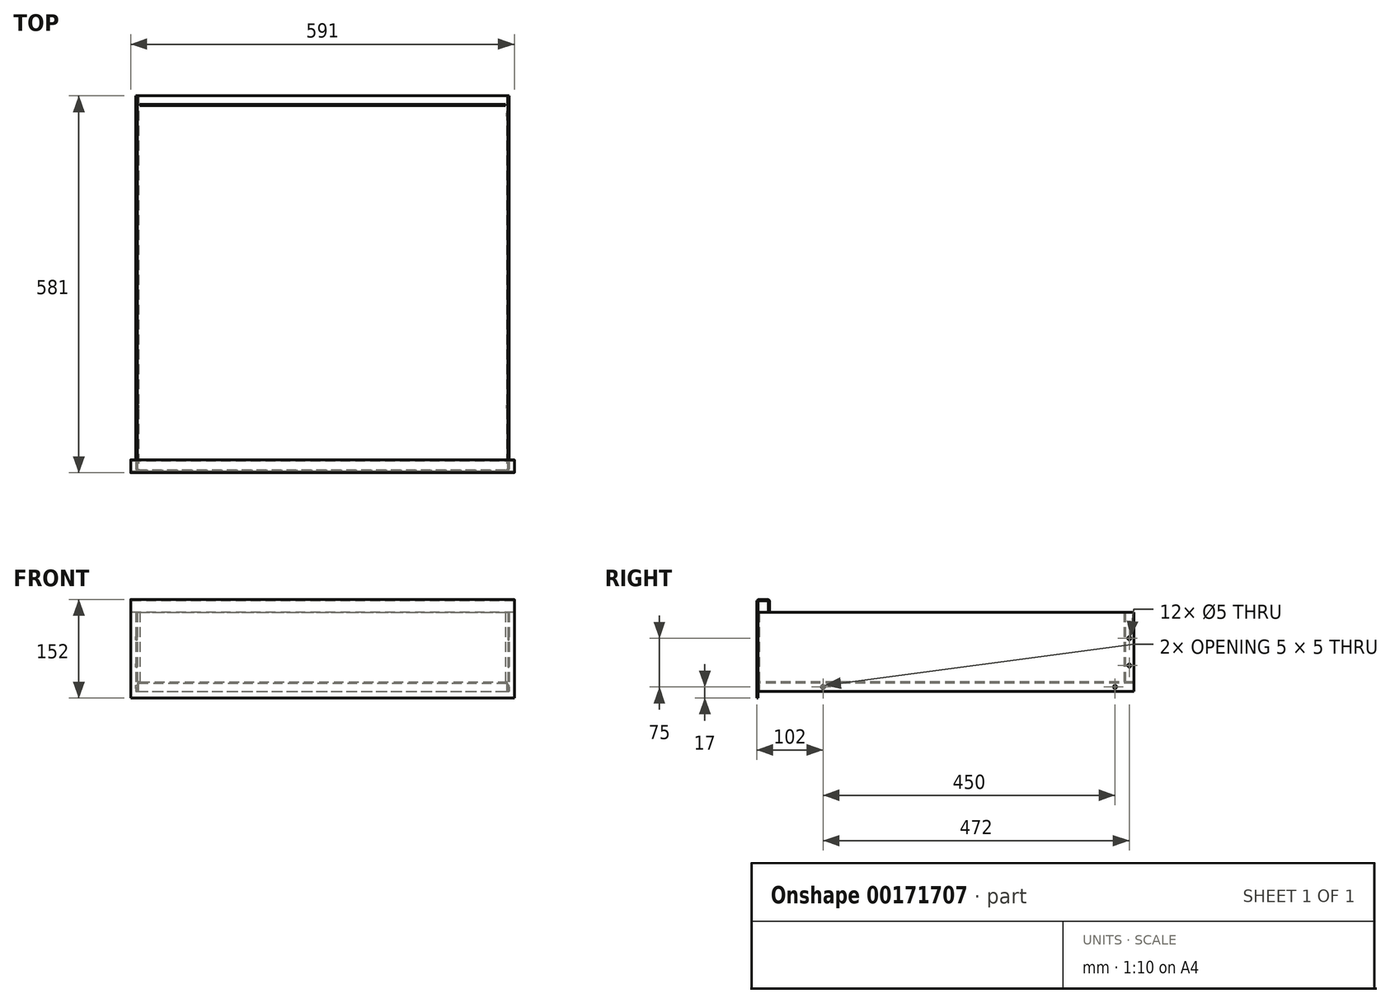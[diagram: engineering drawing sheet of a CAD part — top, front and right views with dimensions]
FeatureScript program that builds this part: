
annotation { "Feature Type Name" : "Feature", "Feature Type Description" : "" }
export const myFeature = defineFeature(function(context is Context, id is Id, definition is map)
    precondition{}
    {
        {
            var Q0;
            Q0=qCreatedBy(makeId("Top.planeOp"),FACE);
            var sketch = newSketch(context, id + "F0", { "sketchPlane" : qUnion([Q0])});
            skLineSegment(sketch, "E0.top", {"start": v(-283.5, -289.5) * mm, "end": v(283.5, -289.5) * mm});
            skLineSegment(sketch, "E0.left", {"start": v(-287.5, 289.5) * mm, "end": v(-287.5, -285.5) * mm});
            skLineSegment(sketch, "E0.right", {"start": v(287.5, 289.5) * mm, "end": v(287.5, -285.5) * mm});
            skPoint(sketch, "E0.middle", {"position": v(0, 0) * mm});
            skLineSegment(sketch, "E1", {"start": v(-287.5, 289.5) * mm, "end": v(287.5, 289.5) * mm, "construction": true});
            skLineSegment(sketch, "E2", {"start": v(-287.5, 289.5) * mm, "end": v(-285.5, 289.5) * mm});
            skLineSegment(sketch, "E3", {"start": v(-285.5, 289.5) * mm, "end": v(-285.5, -287.5) * mm});
            skLineSegment(sketch, "E4", {"start": v(-285.5, -287.5) * mm, "end": v(285.5, -287.5) * mm});
            skLineSegment(sketch, "E5", {"start": v(285.5, -287.5) * mm, "end": v(285.5, 289.5) * mm});
            skPoint(sketch, "E6.visualSharp", {"position": v(-287.5, -289.5) * mm});
            skArc(sketch, "E6.filletArc", {"start": v(-287.5, -285.5) * mm, "mid": v(-286.33, -288.33) * mm, "end": v(-283.5, -289.5) * mm});
            skPoint(sketch, "E7.visualSharp", {"position": v(287.5, -289.5) * mm});
            skArc(sketch, "E7.filletArc", {"start": v(283.5, -289.5) * mm, "mid": v(286.33, -288.33) * mm, "end": v(287.5, -285.5) * mm});
            skLineSegment(sketch, "E8", {"start": v(285.5, 289.5) * mm, "end": v(287.5, 289.5) * mm});
            skSolve(sketch);
        }
        {
            var Q0;
            Q0=makeQuery(id+"F0.imprint","IMPRINT",FACE,{"disambiguationData":[TD([[makeQuery(id+"F0.imprint","IMPRINT",EDGE,{"derivedFrom":sQuery(id+"F0.wireOp",EDGE,"E0.top")}),1.0]])]});
            extrude(context, id + "F1", {"entities" : qUnion([Q0]), "depth" : 122 * mm});
        }
        {
            var Q0;
            Q0=makeQuery(id+"F1.opExtrude","SWEPT_FACE",FACE,{"disambiguationData":[OSD([sQuery(id+"F0.wireOp",EDGE,"E4")])]});
            var sketch = newSketch(context, id + "F2", { "sketchPlane" : qUnion([Q0])});
            skLineSegment(sketch, "E9", {"start": v(-285.5, 0) * mm, "end": v(-285.5, 11) * mm});
            skLineSegment(sketch, "E10", {"start": v(-281.5, 15) * mm, "end": v(281.5, 15) * mm});
            skLineSegment(sketch, "E11", {"start": v(285.5, 11) * mm, "end": v(285.5, 0) * mm});
            skLineSegment(sketch, "E12", {"start": v(285.5, 0) * mm, "end": v(283.5, 0) * mm});
            skLineSegment(sketch, "E13", {"start": v(283.5, 0) * mm, "end": v(283.5, 13) * mm});
            skLineSegment(sketch, "E14", {"start": v(283.5, 13) * mm, "end": v(-283.5, 13) * mm});
            skLineSegment(sketch, "E15", {"start": v(-283.5, 13) * mm, "end": v(-283.5, 0) * mm});
            skLineSegment(sketch, "E16", {"start": v(-283.5, 0) * mm, "end": v(-285.5, 0) * mm});
            skPoint(sketch, "E17.visualSharp", {"position": v(285.5, 15) * mm});
            skArc(sketch, "E17.filletArc", {"start": v(285.5, 11) * mm, "mid": v(284.33, 13.83) * mm, "end": v(281.5, 15) * mm});
            skPoint(sketch, "E18.visualSharp", {"position": v(-285.5, 15) * mm});
            skArc(sketch, "E18.filletArc", {"start": v(-281.5, 15) * mm, "mid": v(-284.33, 13.83) * mm, "end": v(-285.5, 11) * mm});
            skSolve(sketch);
        }
        {
            var Q0;
            Q0=makeQuery(id+"F2.imprint","IMPRINT",FACE,{"disambiguationData":[TD([[makeQuery(id+"F2.imprint","IMPRINT",EDGE,{"derivedFrom":sQuery(id+"F2.wireOp",EDGE,"E9")}),1.0]])]});
            var Q1;
            Q1=makeQuery(id+"F1.opExtrude","SWEPT_FACE",FACE,{"disambiguationData":[OSD([sQuery(id+"F0.wireOp",EDGE,"E2")])]});
            extrude(context, id + "F3", {"entities" : qUnion([Q0]), "endBound" : BoundingType.UP_TO_SURFACE, "endBoundEntityFace" : qUnion([Q1]), "depth" : 25 * mm});
        }
        {
            var Q0;
            Q0=makeQuery(id+"F3.opExtrude","SWEPT_FACE",FACE,{"disambiguationData":[OSD([sQuery(id+"F2.wireOp",EDGE,"E10")])]});
            var sketch = newSketch(context, id + "F4", { "sketchPlane" : qUnion([Q0])});
            skLineSegment(sketch, "E19.0", {"start": v(285.5, -287.5) * mm, "end": v(285.5, 289.5) * mm});
            skLineSegment(sketch, "E20.0", {"start": v(-285.5, 289.5) * mm, "end": v(-285.5, -287.5) * mm});
            skLineSegment(sketch, "E21", {"start": v(-285.5, 289.5) * mm, "end": v(-285.5, 278.5) * mm});
            skLineSegment(sketch, "E22", {"start": v(-281.5, 274.5) * mm, "end": v(281.5, 274.5) * mm});
            skLineSegment(sketch, "E23", {"start": v(285.5, 278.5) * mm, "end": v(285.5, 289.5) * mm});
            skLineSegment(sketch, "E24", {"start": v(285.5, 289.5) * mm, "end": v(283.5, 289.5) * mm});
            skLineSegment(sketch, "E25", {"start": v(283.5, 289.5) * mm, "end": v(283.5, 276.5) * mm});
            skLineSegment(sketch, "E26", {"start": v(283.5, 276.5) * mm, "end": v(-283.5, 276.5) * mm});
            skLineSegment(sketch, "E27", {"start": v(-283.5, 276.5) * mm, "end": v(-283.5, 289.5) * mm});
            skLineSegment(sketch, "E28", {"start": v(-283.5, 289.5) * mm, "end": v(-285.5, 289.5) * mm});
            skPoint(sketch, "E29.visualSharp", {"position": v(285.5, 274.5) * mm});
            skArc(sketch, "E29.filletArc", {"start": v(281.5, 274.5) * mm, "mid": v(284.33, 275.67) * mm, "end": v(285.5, 278.5) * mm});
            skPoint(sketch, "E30.visualSharp", {"position": v(-285.5, 274.5) * mm});
            skArc(sketch, "E30.filletArc", {"start": v(-285.5, 278.5) * mm, "mid": v(-284.33, 275.67) * mm, "end": v(-281.5, 274.5) * mm});
            skSolve(sketch);
        }
        {
            var Q0;
            {var subQ0=sQuery(id+"F4.wireOp",EDGE,"E22");Q0=makeQuery(id+"F4.imprint","IMPRINT",FACE,{"disambiguationData":[TD([[makeQuery(id+"F4.imprint","IMPRINT",EDGE,{"derivedFrom":subQ0}),1.0]])]});}
            var Q1;
            Q1=makeQuery(id+"F4.imprint","IMPRINT",FACE,{"disambiguationData":[TD([[makeQuery(id+"F4.imprint","IMPRINT",EDGE,{"derivedFrom":sQuery(id+"F4.wireOp",EDGE,"E21")}),1.0]])]});
            var Q2;
            Q2=makeQuery(id+"F4.imprint","IMPRINT",FACE,{"disambiguationData":[TD([[makeQuery(id+"F4.imprint","IMPRINT",EDGE,{"derivedFrom":sQuery(id+"F4.wireOp",EDGE,"E23")}),1.0]])]});
            var Q3;
            Q3=makeQuery(id+"F1.opExtrude","CAP_FACE",FACE,{"disambiguationData":[OSD([sQuery(id+"F0.wireOp",EDGE,"E0.top"),sQuery(id+"F0.wireOp",EDGE,"E0.left"),sQuery(id+"F0.wireOp",EDGE,"E0.right"),sQuery(id+"F0.wireOp",EDGE,"E2"),sQuery(id+"F0.wireOp",EDGE,"E3"),sQuery(id+"F0.wireOp",EDGE,"E4"),sQuery(id+"F0.wireOp",EDGE,"E5"),sQuery(id+"F0.wireOp",EDGE,"E6.filletArc"),sQuery(id+"F0.wireOp",EDGE,"E7.filletArc"),sQuery(id+"F0.wireOp",EDGE,"E8")])],"isStart":false});
            extrude(context, id + "F5", {"entities" : qUnion([Q0, Q1, Q2]), "endBound" : BoundingType.UP_TO_SURFACE, "endBoundEntityFace" : qUnion([Q3]), "depth" : 25 * mm});
        }
        {
            var Q0;
            Q0=makeQuery(id+"F1.opExtrude","SWEPT_FACE",FACE,{"disambiguationData":[OSD([sQuery(id+"F0.wireOp",EDGE,"E0.right")])]});
            var sketch = newSketch(context, id + "F6", { "sketchPlane" : qUnion([Q0])});
            skLineSegment(sketch, "E31.0", {"start": v(-289.5, 122) * mm, "end": v(-289.5, 0) * mm});
            skLineSegment(sketch, "E32", {"start": v(-374.1, 7) * mm, "end": v(407.57, 7) * mm, "construction": true});
            skLineSegment(sketch, "E33", {"start": v(282.5, -59.87) * mm, "end": v(282.5, 378.9) * mm, "construction": true});
            skPoint(sketch, "E34", {"position": v(-189.5, 7) * mm});
            skPoint(sketch, "E35", {"position": v(260.5, 7) * mm});
            skPoint(sketch, "E36", {"position": v(282.5, 82) * mm});
            skPoint(sketch, "E37", {"position": v(282.5, 40) * mm});
            skSolve(sketch);
        }
        {
            var Q0;
            Q0=sQuery(id+"F6.wireOp",VERTEX,"E37");
            var Q1;
            Q1=sQuery(id+"F6.wireOp",VERTEX,"E35");
            var Q2;
            Q2=sQuery(id+"F6.wireOp",VERTEX,"E36");
            var Q3;
            Q3=sQuery(id+"F6.wireOp",VERTEX,"E34");
            var Q4;
            Q4=makeQuery(id+"F1.opExtrude","SWEPT_BODY",BODY,{"disambiguationData":[OSD([sQuery(id+"F0.wireOp",EDGE,"E0.top"),sQuery(id+"F0.wireOp",EDGE,"E0.left"),sQuery(id+"F0.wireOp",EDGE,"E0.right"),sQuery(id+"F0.wireOp",EDGE,"E2"),sQuery(id+"F0.wireOp",EDGE,"E3"),sQuery(id+"F0.wireOp",EDGE,"E4"),sQuery(id+"F0.wireOp",EDGE,"E5"),sQuery(id+"F0.wireOp",EDGE,"E6.filletArc"),sQuery(id+"F0.wireOp",EDGE,"E7.filletArc"),sQuery(id+"F0.wireOp",EDGE,"E8")])]});
            var Q5;
            Q5=makeQuery(id+"F3.opExtrude","SWEPT_BODY",BODY,{"disambiguationData":[OSD([sQuery(id+"F2.wireOp",EDGE,"E9"),sQuery(id+"F2.wireOp",EDGE,"E10"),sQuery(id+"F2.wireOp",EDGE,"E11"),sQuery(id+"F2.wireOp",EDGE,"E12"),sQuery(id+"F2.wireOp",EDGE,"E13"),sQuery(id+"F2.wireOp",EDGE,"E14"),sQuery(id+"F2.wireOp",EDGE,"E15"),sQuery(id+"F2.wireOp",EDGE,"E16"),sQuery(id+"F2.wireOp",EDGE,"E17.filletArc"),sQuery(id+"F2.wireOp",EDGE,"E18.filletArc")])]});
            var Q6;
            Q6=makeQuery(id+"F5.opExtrude","SWEPT_BODY",BODY,{"disambiguationData":[OSD([sQuery(id+"F4.wireOp",EDGE,"E21"),sQuery(id+"F4.wireOp",EDGE,"E22"),sQuery(id+"F4.wireOp",EDGE,"E23"),sQuery(id+"F4.wireOp",EDGE,"E24"),sQuery(id+"F4.wireOp",EDGE,"E25"),sQuery(id+"F4.wireOp",EDGE,"E26"),sQuery(id+"F4.wireOp",EDGE,"E27"),sQuery(id+"F4.wireOp",EDGE,"E28"),sQuery(id+"F4.wireOp",EDGE,"E29.filletArc"),sQuery(id+"F4.wireOp",EDGE,"E30.filletArc")])]});
            hole(context, id + "F7", {"style" : HoleStyle.C_SINK, "endStyle" : HoleEndStyle.BLIND, "holeDiameter" : 5 * mm, "cSinkDiameter" : 5 * mm, "cSinkAngle" : 90 * degree, "holeDepth" : 2000 * mm, "startFromSketch" : true, "locations" : qUnion([Q0, Q1, Q2, Q3]), "scope" : qUnion([Q4, Q5, Q6])});
        }
        {
            var Q0;
            Q0=qCreatedBy(makeId("Right.planeOp"),FACE);
            var sketch = newSketch(context, id + "F8", { "sketchPlane" : qUnion([Q0])});
            skPoint(sketch, "E38.0", {"position": v(-289.5, 122) * mm});
            skPoint(sketch, "E39.0", {"position": v(-289.5, 0) * mm});
            skLineSegment(sketch, "E40.0", {"start": v(289.5, 122) * mm, "end": v(-285.5, 122) * mm});
            skLineSegment(sketch, "E41", {"start": v(-289.5, 122) * mm, "end": v(-289.5, 140) * mm});
            skLineSegment(sketch, "E42", {"start": v(-289.5, 140) * mm, "end": v(-273.5, 140) * mm});
            skLineSegment(sketch, "E43", {"start": v(-273.5, 140) * mm, "end": v(-273.5, 122) * mm});
            skLineSegment(sketch, "E44", {"start": v(-273.5, 122) * mm, "end": v(-271.5, 122) * mm});
            skLineSegment(sketch, "E45", {"start": v(-271.5, 122) * mm, "end": v(-271.5, 138) * mm});
            skLineSegment(sketch, "E46", {"start": v(-275.5, 142) * mm, "end": v(-287.5, 142) * mm});
            skLineSegment(sketch, "E47", {"start": v(-291.5, 138) * mm, "end": v(-291.5, 122) * mm});
            skLineSegment(sketch, "E48", {"start": v(-291.5, 122) * mm, "end": v(-289.5, 122) * mm});
            skPoint(sketch, "E49.visualSharp", {"position": v(-291.5, 142) * mm});
            skArc(sketch, "E49.filletArc", {"start": v(-287.5, 142) * mm, "mid": v(-290.33, 140.83) * mm, "end": v(-291.5, 138) * mm});
            skPoint(sketch, "E50.visualSharp", {"position": v(-271.5, 142) * mm});
            skArc(sketch, "E50.filletArc", {"start": v(-271.5, 138) * mm, "mid": v(-272.67, 140.83) * mm, "end": v(-275.5, 142) * mm});
            skLineSegment(sketch, "E51", {"start": v(-289.5, 0) * mm, "end": v(-289.5, -10) * mm});
            skLineSegment(sketch, "E52", {"start": v(-289.5, -10) * mm, "end": v(-291.5, -10) * mm});
            skLineSegment(sketch, "E53", {"start": v(-291.5, -10) * mm, "end": v(-291.5, 0) * mm});
            skLineSegment(sketch, "E54", {"start": v(-291.5, 0) * mm, "end": v(-289.5, 0) * mm});
            skLineSegment(sketch, "E55", {"start": v(-289.5, 0) * mm, "end": v(-289.5, 122) * mm});
            skLineSegment(sketch, "E56", {"start": v(-291.5, 122) * mm, "end": v(-291.5, 0) * mm});
            skSolve(sketch);
        }
        {
            var Q0;
            Q0=makeQuery(id+"F8.imprint","IMPRINT",FACE,{"disambiguationData":[TD([[makeQuery(id+"F8.imprint","IMPRINT",EDGE,{"derivedFrom":sQuery(id+"F8.wireOp",EDGE,"E51")}),-1.0]])]});
            var Q1;
            Q1=makeQuery(id+"F8.imprint","IMPRINT",FACE,{"disambiguationData":[TD([[makeQuery(id+"F8.imprint","IMPRINT",EDGE,{"derivedFrom":sQuery(id+"F8.wireOp",EDGE,"E48")}),-1.0]])]});
            var Q2;
            Q2=makeQuery(id+"F8.imprint","IMPRINT",FACE,{"disambiguationData":[TD([[makeQuery(id+"F8.imprint","IMPRINT",EDGE,{"derivedFrom":sQuery(id+"F8.wireOp",EDGE,"E41")}),1.0]])]});
            extrude(context, id + "F9", {"entities" : qUnion([Q0, Q1, Q2]), "endBound" : BoundingType.SYMMETRIC, "depth" : 591 * mm});
        }
    });
